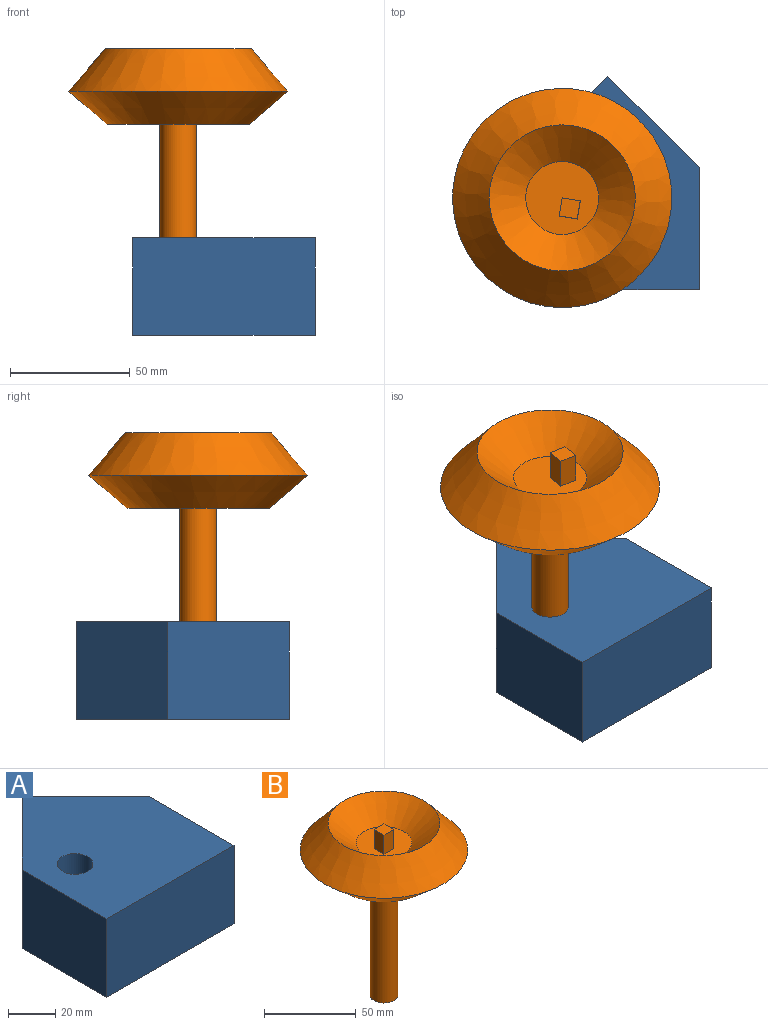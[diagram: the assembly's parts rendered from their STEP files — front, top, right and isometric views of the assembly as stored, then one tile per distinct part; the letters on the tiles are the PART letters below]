
ASSEMBLY  parts=2 mates=1
PART A: 8 faces, bbox 76.2x88.9x40.6 mm
  f0: plane 50.8x40.64mm, normal (1,0,0), area 2064.5mm2, adj f1,f4,f5,f6
  f1: plane 40.64x38.1mm, normal (0.71,0.71,0), area 2189.7mm2, adj f0,f2,f5,f6
  f2: plane 40.64x38.1mm, normal (-0.71,0.71,0), area 2189.7mm2, adj f1,f3,f5,f6
  f3: plane 50.8x40.64mm, normal (-1,0,0), area 2064.5mm2, adj f2,f4,f5,f6
  f4: plane 76.2x40.64mm, normal (0,-1,0), area 3096.8mm2, adj f0,f3,f5,f6
  f5: plane 88.9x76.2mm, normal (0,0,1), area 5140.2mm2, adj f0,f1,f2,f3,f4,f7
  f6: plane 88.9x76.2mm, normal (0,0,-1), area 5140.2mm2, adj f0,f1,f2,f3,f4,f7
  f7: cylinder r=7.62mm len=40.64mm, axis (0,0,1), area 1945.8mm2, adj f5,f6
PART B: 13 faces, bbox 91.4x91.4x114.7 mm
  f0: plane 15.24x15.24mm, normal (0,0,-1), area 182.4mm2, adj f1
  f1: cylinder r=7.62mm len=96.88mm, axis (0,0,-1), area 4638.5mm2, adj f0,f2
  f2: plane 35.56x35.56mm, normal (0,0,-1), area 810.7mm2, adj f1,f3
  f3: cone r=29.61mm half-angle=40.6deg, axis (0,0,-1), area 2707.3mm2, adj f2,f4
  f4: cone r=45.72mm half-angle=49.4deg, axis (0,0,1), area 5020.6mm2, adj f3,f5
  f5: cone r=30.48mm half-angle=40.6deg, axis (0,0,-1), area 5605.9mm2, adj f4,f6
  f6: cone r=15.24mm half-angle=49.4deg, axis (0,0,1), area 2883.1mm2, adj f5,f7
  f7: plane 30.48x30.48mm, normal (0,0,1), area 671.6mm2, adj f6,f8,f9,f10,f11
  f8: plane 12.7x7.62mm, normal (0,-1,0), area 96.8mm2, adj f7,f9,f11,f12
  f9: plane 12.7x7.62mm, normal (1,0,0), area 96.8mm2, adj f7,f8,f10,f12
  f10: plane 12.7x7.62mm, normal (0,1,0), area 96.8mm2, adj f7,f9,f11,f12
  f11: plane 12.7x7.62mm, normal (-1,0,0), area 96.8mm2, adj f7,f8,f10,f12
  f12: plane 7.62x7.62mm, normal (0,0,1), area 58.1mm2, adj f8,f9,f10,f11
PLACE A t=(-4.68,0.84,5.32)mm fixed
PLACE B rot(axis=(0,0,1),80.4deg) t=(14.37,38.94,91.49)mm
MATE revolute B.f1 <-> A.f7  axis (0,0,-1) through (14.37,38.94,58.66)mm
